# Revit family: Pedro-empty-NoHosted-IT-en
name_source: partatom
category: Electrical Equipment
units: mm (PartAtom-declared; Revit-internal decimal feet)

## family parameters
Always vertical = Yes
Cut with Voids When Loaded = No
Panel Configuration = Two Columns, Circuits Across
Part Type = Panelboard
Room Calculation Point = No
Round Connector Dimension = Use Diameter
Shared = No
Work Plane-Based = Yes

## types (2) — shared parameters
Default Elevation = 1219 mm
EF000003 - Mounting method = EV000384 - Surface mounted (plaster)
EF000007 - Colour = EV000270 - Grey
EF000008 - Width = 265 mm  [stored 0.869423 ft]
EF000040 - Height = 303 mm  [stored 0.994094 ft]
EF000049 - Depth = 167 mm  [stored 0.5479 ft]
EF000116 - RAL-number = 7035
EF000118 - With mounting plate = No
EF000339 - Type of cover = EV004216 - Door
EF001062 - EMC-version = Yes
EF001088 - Extension possible = Yes
EF001131 - Internal depth = 137 mm
EF001134 - DIN-rail = No
EF001596 - Material housing = EV000139 - Plastic
EF004462 - Type of closure = EV000154 - Other
EF005474 - Degree of protection (IP) = EV006422 - IP66
EF006306 - With lock = Yes
EF009212 - Cover model = EV000116 - Closed
EF015776 - Earthing terminal block = No
EF015777 - Neutral terminal block = No
EF015941 - Signal passing door = No
HG000002 - With door or cover = Yes
HG000003 - Range = Pedro
HG000005 - Thickness = 3 mm  [stored 0.00984252 ft]
HG000006 - Flush mounted = No
HG000009 - Double swing door = No
HG000010 - Asymmetric doors = No
HG000011 - Empty rows from bottom = No
Manufacturer = Hager
Type Comments = Pedro
zero-valued in all types: EF000218 - Built-in depth, EF000266 - Number of rows, EF000332 - Built-in height, EF000846 - Built-in width, EF002950 - Width in number of modular spacings, HG000001 - Number of columns, HG000007 - Number of empty columns, HG000008 - Number of empty rows

## per-type parameters (varying)
| type | EF006244 - Transparent cover/door | HG000004 - Manufacturer reference | Model |
| Surface mounted IP66 W264.7 H302.8 D167  Modular spacings - B04601 | No | B04601 | B04601 |
| Surface mounted IP66 W264.7 H302.8 D167  Modular spacings - B04621 | Yes | B04621 | B04621 |

note: [stored X ft] marks values corroborated as IEEE doubles in the binary element streams (Revit-internal decimal feet)

## geometry (parser evidence)
native form markers: Sweep x16
no freeform markers — native parametric forms only
